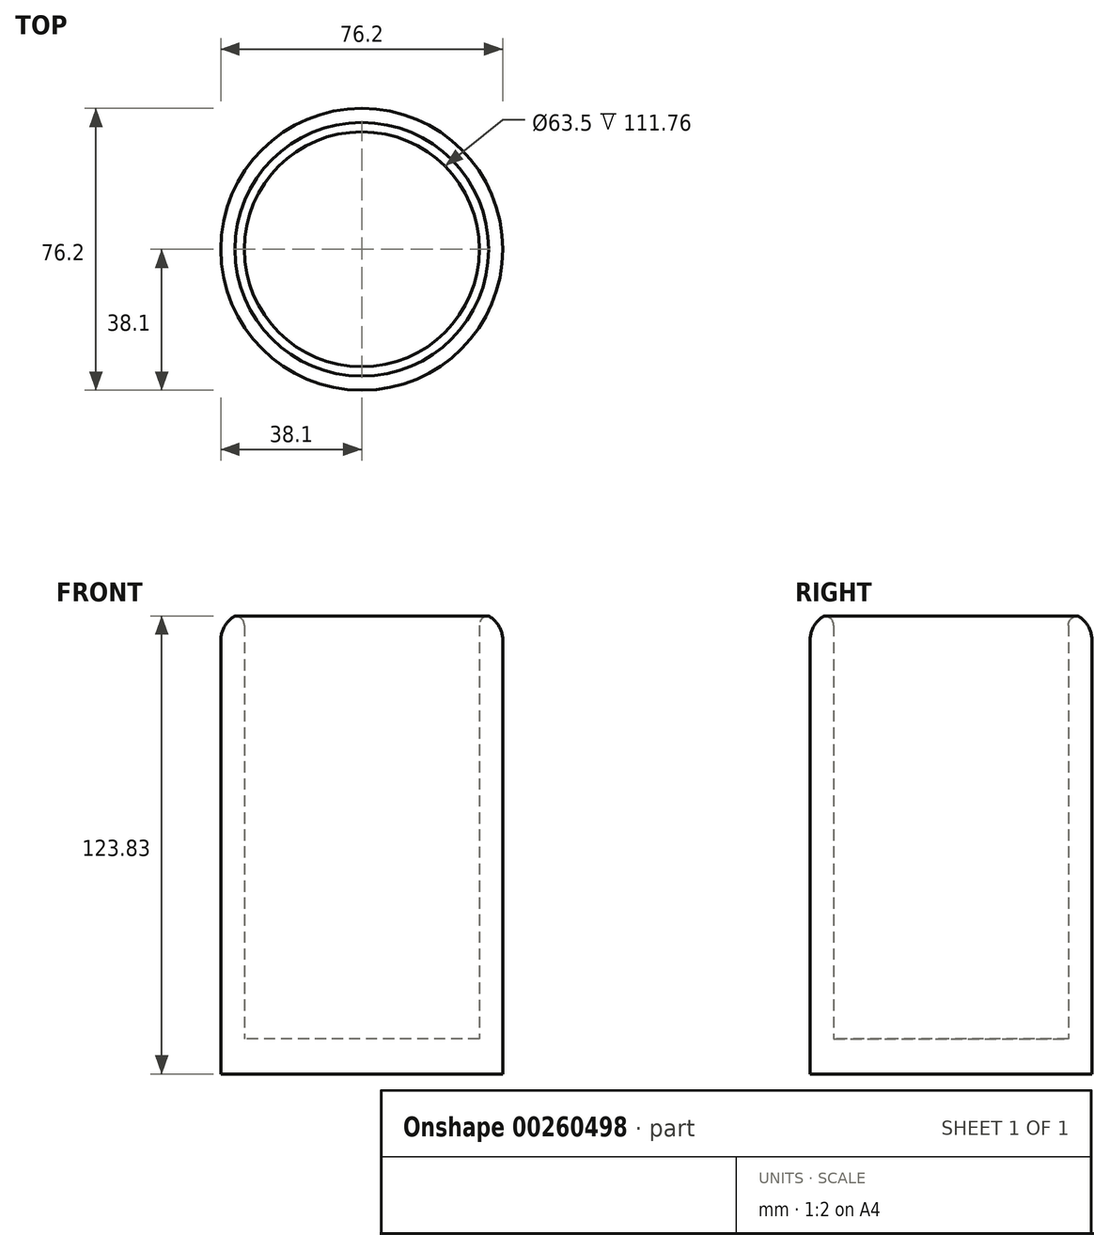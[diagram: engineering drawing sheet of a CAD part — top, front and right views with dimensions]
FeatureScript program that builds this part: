
annotation { "Feature Type Name" : "Feature", "Feature Type Description" : "" }
export const myFeature = defineFeature(function(context is Context, id is Id, definition is map)
    precondition{}
    {
        {
            var Q0;
            Q0=qCreatedBy(makeId("Top.planeOp"),FACE);
            var sketch = newSketch(context, id + "F0", { "sketchPlane" : qUnion([Q0])});
            skCircle(sketch, "E0", {"center": v(0, 0) * mm, "radius": 38.1 * mm});
            skCircle(sketch, "E1", {"center": v(0, 0) * mm, "radius": 31.75 * mm});
            skSolve(sketch);
        }
        {
            var Q0;
            Q0=makeQuery(id+"F0.imprint","IMPRINT",FACE,{"disambiguationData":[TD([[makeQuery(id+"F0.imprint","IMPRINT",EDGE,{"derivedFrom":sQuery(id+"F0.wireOp",EDGE,"E0")}),1.0]])]});
            extrude(context, id + "F1", {"entities" : qUnion([Q0]), "depth" : 123.82 * mm});
        }
        {
            var Q0;
            Q0=makeQuery(id+"F0.imprint","IMPRINT",FACE,{"disambiguationData":[TD([[makeQuery(id+"F0.imprint","IMPRINT",EDGE,{"derivedFrom":sQuery(id+"F0.wireOp",EDGE,"E1")}),1.0]])]});
            extrude(context, id + "F2", {"entities" : qUnion([Q0]), "operationType" : NewBodyOperationType.ADD, "depth" : 9.52 * mm});
        }
        {
            var Q0;
            Q0=makeQuery(id+"F1.opExtrude","CAP_EDGE",EDGE,{"disambiguationData":[OSD([sQuery(id+"F0.wireOp",EDGE,"E1")])],"isStart":false});
            fillet(context, id + "F3", {"entities" : qUnion([Q0]), "radius" : 2.54 * mm, "tangentPropagation" : true, "allowEdgeOverflow" : false});
        }
        {
            var Q0;
            Q0=makeQuery(id+"F1.opExtrude","CAP_EDGE",EDGE,{"disambiguationData":[OSD([sQuery(id+"F0.wireOp",EDGE,"E0")])],"isStart":false});
            fillet(context, id + "F4", {"entities" : qUnion([Q0]), "radius" : 7.62 * mm, "tangentPropagation" : true, "allowEdgeOverflow" : false});
        }
    });
